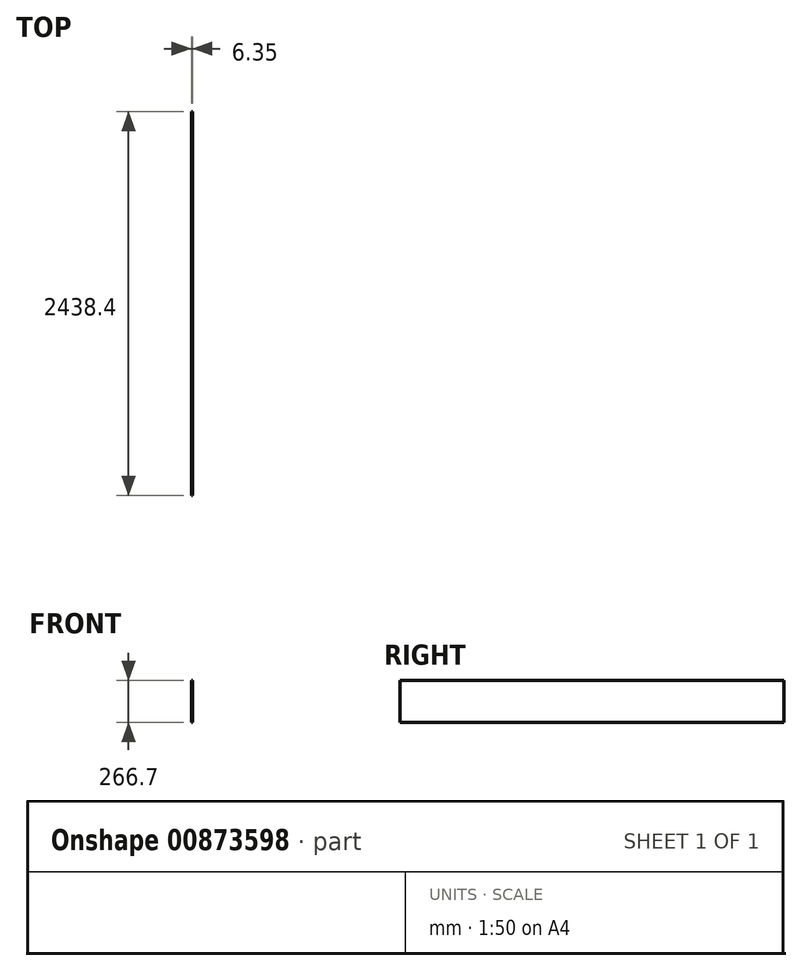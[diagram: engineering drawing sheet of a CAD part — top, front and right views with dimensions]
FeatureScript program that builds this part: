
annotation { "Feature Type Name" : "Feature", "Feature Type Description" : "" }
export const myFeature = defineFeature(function(context is Context, id is Id, definition is map)
    precondition{}
    {
        {
            var Q0;
            Q0=qCreatedBy(makeId("Front.planeOp"),FACE);
            var sketch = newSketch(context, id + "F0", { "sketchPlane" : qUnion([Q0])});
            skLineSegment(sketch, "E0.bottom", {"start": v(0, 0) * mm, "end": v(6.35, 0) * mm});
            skLineSegment(sketch, "E0.top", {"start": v(0, 266.7) * mm, "end": v(6.35, 266.7) * mm});
            skLineSegment(sketch, "E0.left", {"start": v(0, 0) * mm, "end": v(0, 266.7) * mm});
            skLineSegment(sketch, "E0.right", {"start": v(6.35, 0) * mm, "end": v(6.35, 266.7) * mm});
            skSolve(sketch);
        }
        {
            var Q0;
            Q0 = qSketchRegion(id + "F0", true);
            extrude(context, id + "F1", {"entities" : qUnion([Q0]), "oppositeDirection" : true, "depth" : 2438.4 * mm, "offsetDistance" : 25.4 * mm});
        }
    });
